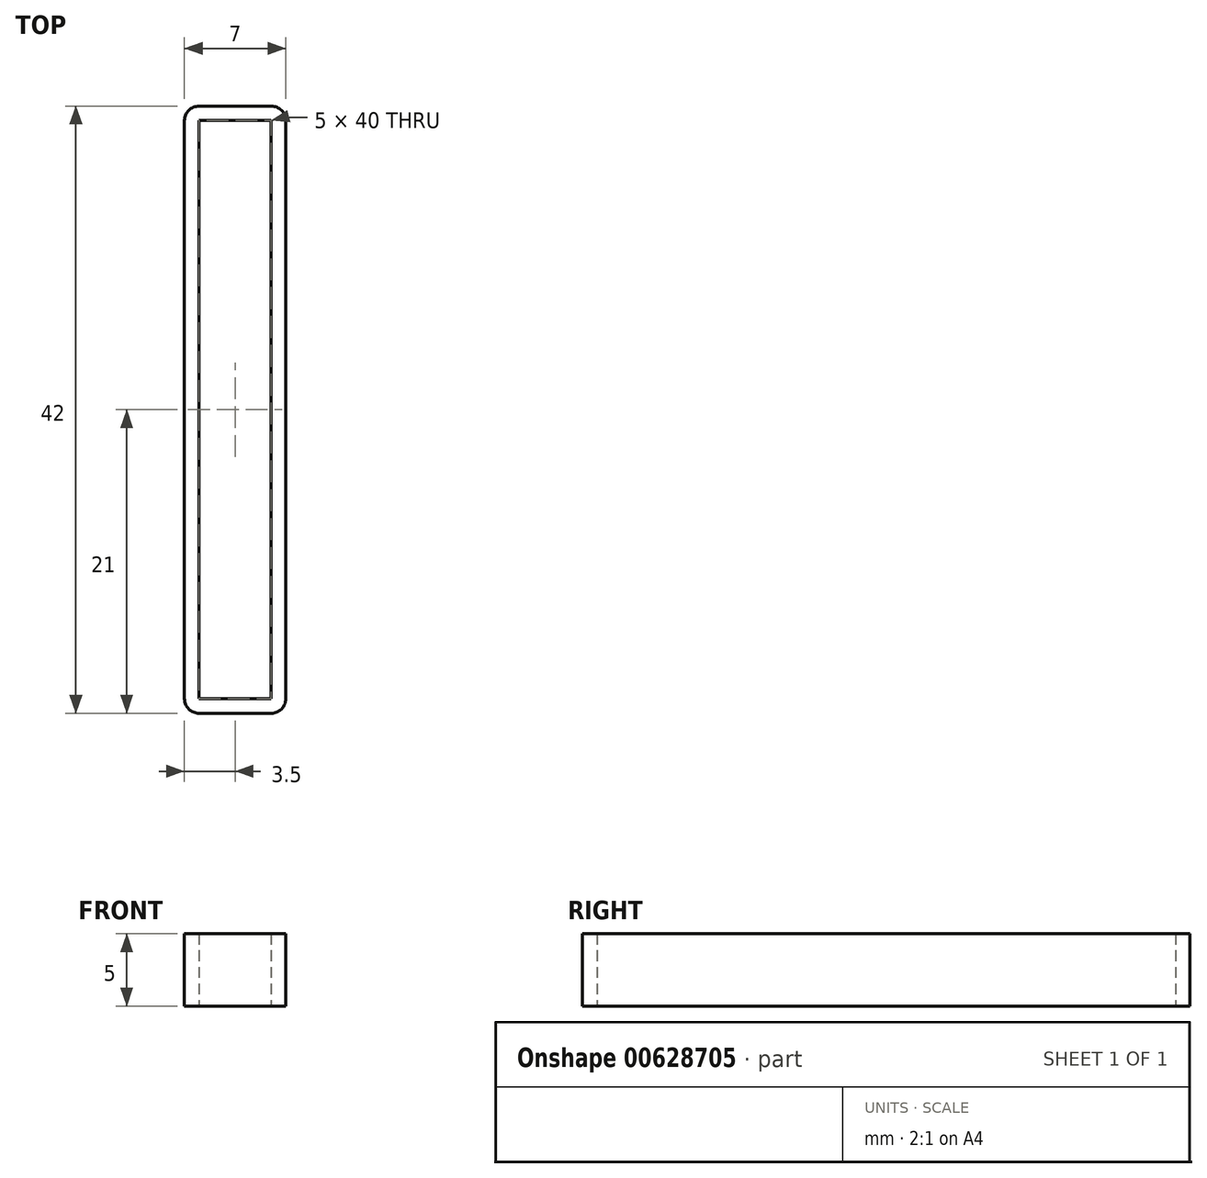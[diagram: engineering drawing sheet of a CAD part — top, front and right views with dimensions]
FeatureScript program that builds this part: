
annotation { "Feature Type Name" : "Feature", "Feature Type Description" : "" }
export const myFeature = defineFeature(function(context is Context, id is Id, definition is map)
    precondition{}
    {
        {
            var Q0;
            Q0=qCreatedBy(makeId("Top.planeOp"),FACE);
            var sketch = newSketch(context, id + "F0", { "sketchPlane" : qUnion([Q0])});
            skLineSegment(sketch, "E0.bottom", {"start": v(2.5, -21) * mm, "end": v(-2.5, -21) * mm});
            skLineSegment(sketch, "E0.top", {"start": v(2.5, 21) * mm, "end": v(-2.5, 21) * mm});
            skLineSegment(sketch, "E0.left", {"start": v(3.5, -20) * mm, "end": v(3.5, 20) * mm});
            skLineSegment(sketch, "E0.right", {"start": v(-3.5, -20) * mm, "end": v(-3.5, 20) * mm});
            skPoint(sketch, "E0.middle", {"position": v(0, 0) * mm});
            skPoint(sketch, "E1.visualSharp", {"position": v(-3.5, 21) * mm});
            skArc(sketch, "E1.filletArc", {"start": v(-2.5, 21) * mm, "mid": v(-3.2, 20.7) * mm, "end": v(-3.5, 20) * mm});
            skPoint(sketch, "E2.visualSharp", {"position": v(3.5, 21) * mm});
            skArc(sketch, "E2.filletArc", {"start": v(3.5, 20) * mm, "mid": v(3.2, 20.7) * mm, "end": v(2.5, 21) * mm});
            skPoint(sketch, "E3.visualSharp", {"position": v(3.5, -21) * mm});
            skArc(sketch, "E3.filletArc", {"start": v(2.5, -21) * mm, "mid": v(3.2, -20.7) * mm, "end": v(3.5, -20) * mm});
            skPoint(sketch, "E4.visualSharp", {"position": v(-3.5, -21) * mm});
            skArc(sketch, "E4.filletArc", {"start": v(-3.5, -20) * mm, "mid": v(-3.2, -20.7) * mm, "end": v(-2.5, -21) * mm});
            skLineSegment(sketch, "E5", {"start": v(2.5, 20) * mm, "end": v(-2.5, 20) * mm});
            skLineSegment(sketch, "E6", {"start": v(-2.5, -20) * mm, "end": v(2.5, -20) * mm});
            skLineSegment(sketch, "E7", {"start": v(2.5, -20) * mm, "end": v(2.5, 20) * mm});
            skLineSegment(sketch, "E8", {"start": v(-2.5, 20) * mm, "end": v(-2.5, -20) * mm});
            skSolve(sketch);
        }
        {
            var Q0;
            Q0 = qSketchRegion(id + "F0", true);
            extrude(context, id + "F1", {"entities" : qUnion([Q0]), "endBound" : BoundingType.SYMMETRIC, "depth" : 5 * mm, "offsetDistance" : 25 * mm});
        }
    });
